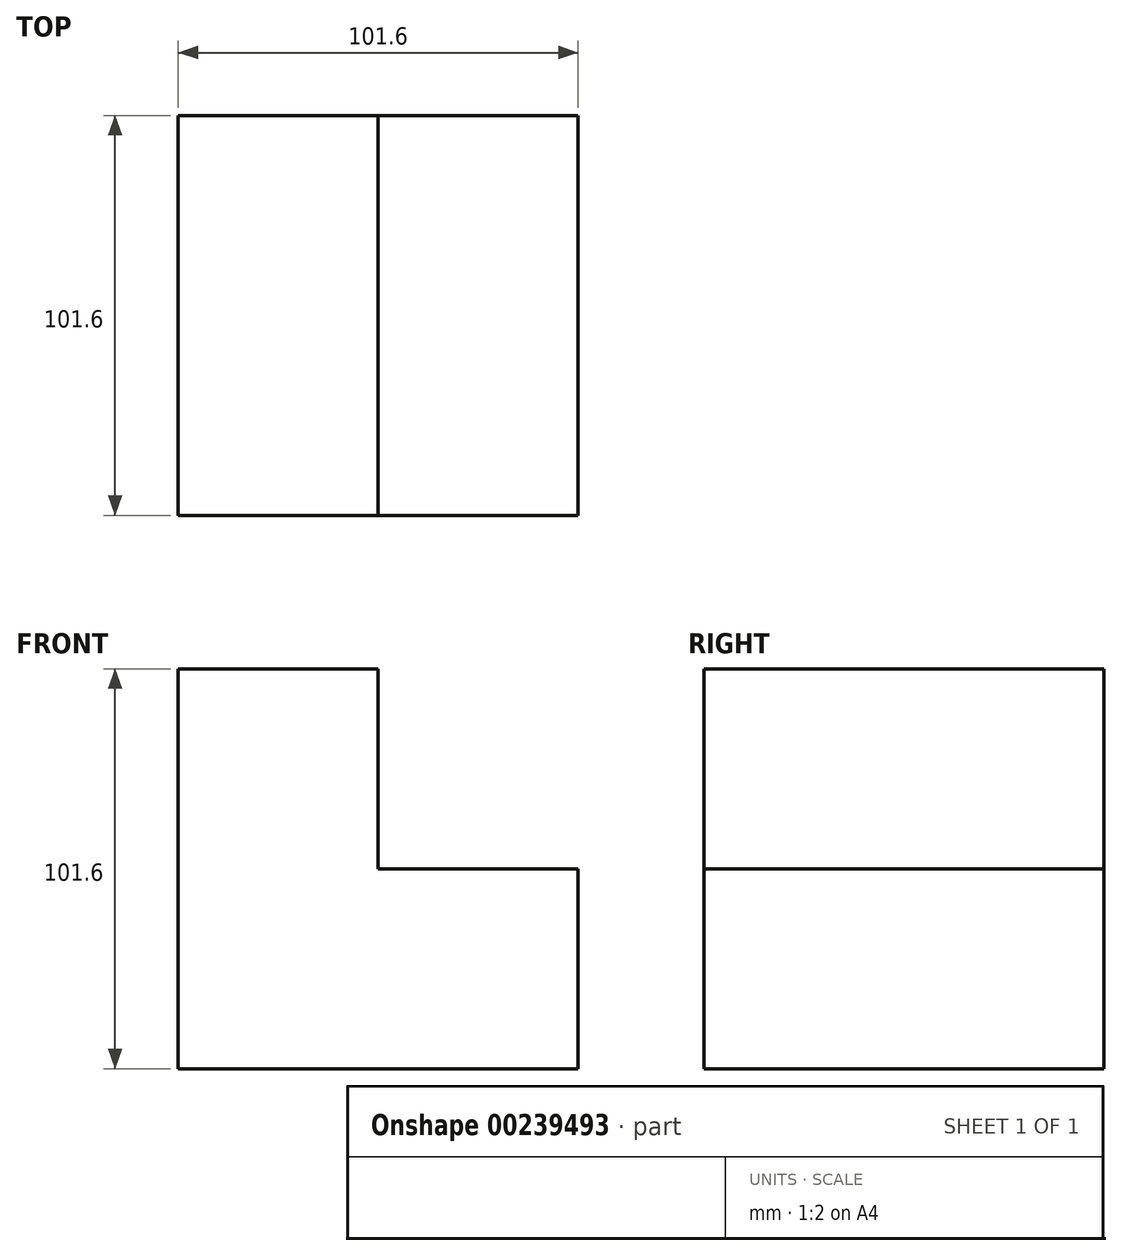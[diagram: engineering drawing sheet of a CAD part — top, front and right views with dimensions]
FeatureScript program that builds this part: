
annotation { "Feature Type Name" : "Feature", "Feature Type Description" : "" }
export const myFeature = defineFeature(function(context is Context, id is Id, definition is map)
    precondition{}
    {
        {
            var Q0;
            Q0=qCreatedBy(makeId("Front.planeOp"),FACE);
            var sketch = newSketch(context, id + "F0", { "sketchPlane" : qUnion([Q0])});
            skLineSegment(sketch, "E0.bottom", {"start": v(50.8, 50.8) * mm, "end": v(-50.8, 50.8) * mm});
            skLineSegment(sketch, "E0.top", {"start": v(50.8, -50.8) * mm, "end": v(-50.8, -50.8) * mm});
            skLineSegment(sketch, "E0.left", {"start": v(50.8, 50.8) * mm, "end": v(50.8, -50.8) * mm});
            skLineSegment(sketch, "E0.right", {"start": v(-50.8, 50.8) * mm, "end": v(-50.8, -50.8) * mm});
            skPoint(sketch, "E0.middle", {"position": v(0, 0) * mm});
            skSolve(sketch);
        }
        {
            var Q0;
            Q0 = qSketchRegion(id + "F0", true);
            extrude(context, id + "F1", {"entities" : qUnion([Q0]), "depth" : 101.6 * mm});
        }
        {
            var Q0;
            Q0=qCreatedBy(makeId("Front.planeOp"),FACE);
            var sketch = newSketch(context, id + "F2", { "sketchPlane" : qUnion([Q0])});
            skLineSegment(sketch, "E1.bottom", {"start": v(0, 0) * mm, "end": v(50.8, 0) * mm});
            skLineSegment(sketch, "E1.top", {"start": v(0, 50.8) * mm, "end": v(50.8, 50.8) * mm});
            skLineSegment(sketch, "E1.left", {"start": v(0, 0) * mm, "end": v(0, 50.8) * mm});
            skLineSegment(sketch, "E1.right", {"start": v(50.8, 0) * mm, "end": v(50.8, 50.8) * mm});
            skSolve(sketch);
        }
        {
            var Q0;
            Q0 = qSketchRegion(id + "F2", true);
            extrude(context, id + "F3", {"entities" : qUnion([Q0]), "operationType" : NewBodyOperationType.REMOVE, "depth" : 134.37 * mm});
        }
    });
